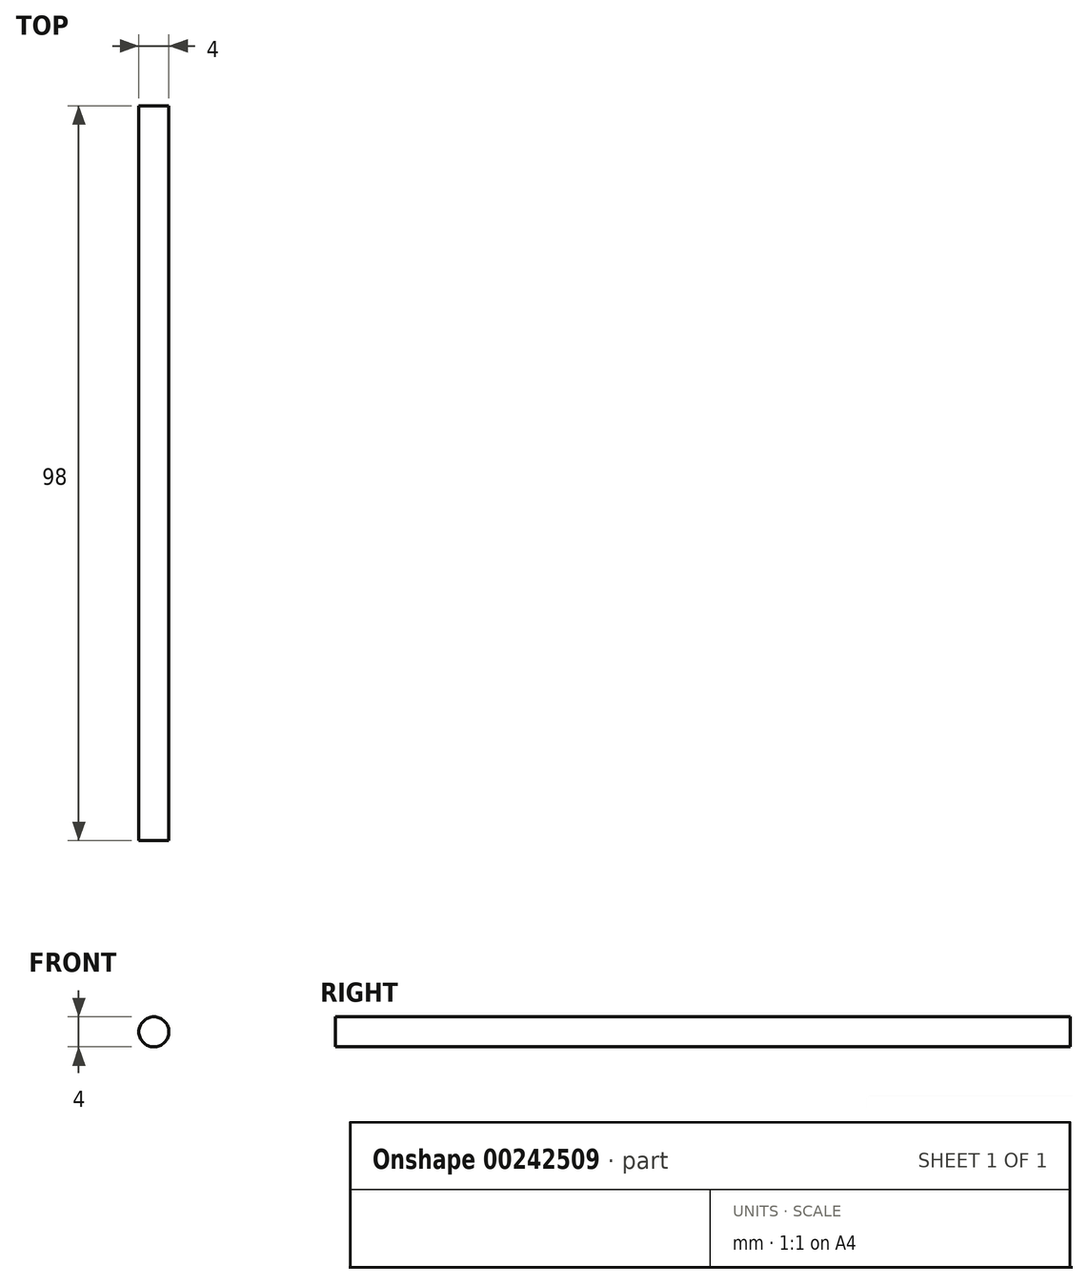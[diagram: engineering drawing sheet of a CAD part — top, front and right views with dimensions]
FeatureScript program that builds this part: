
annotation { "Feature Type Name" : "Feature", "Feature Type Description" : "" }
export const myFeature = defineFeature(function(context is Context, id is Id, definition is map)
    precondition{}
    {
        {
            var Q0;
            Q0=qCreatedBy(makeId("Front.planeOp"),FACE);
            var sketch = newSketch(context, id + "F0", { "sketchPlane" : qUnion([Q0])});
            skCircle(sketch, "E0", {"center": v(0, 0) * mm, "radius": 2 * mm});
            skSolve(sketch);
        }
        {
            var Q0;
            Q0 = qSketchRegion(id + "F0", true);
            extrude(context, id + "F1", {"entities" : qUnion([Q0]), "depth" : 98 * mm});
        }
    });
